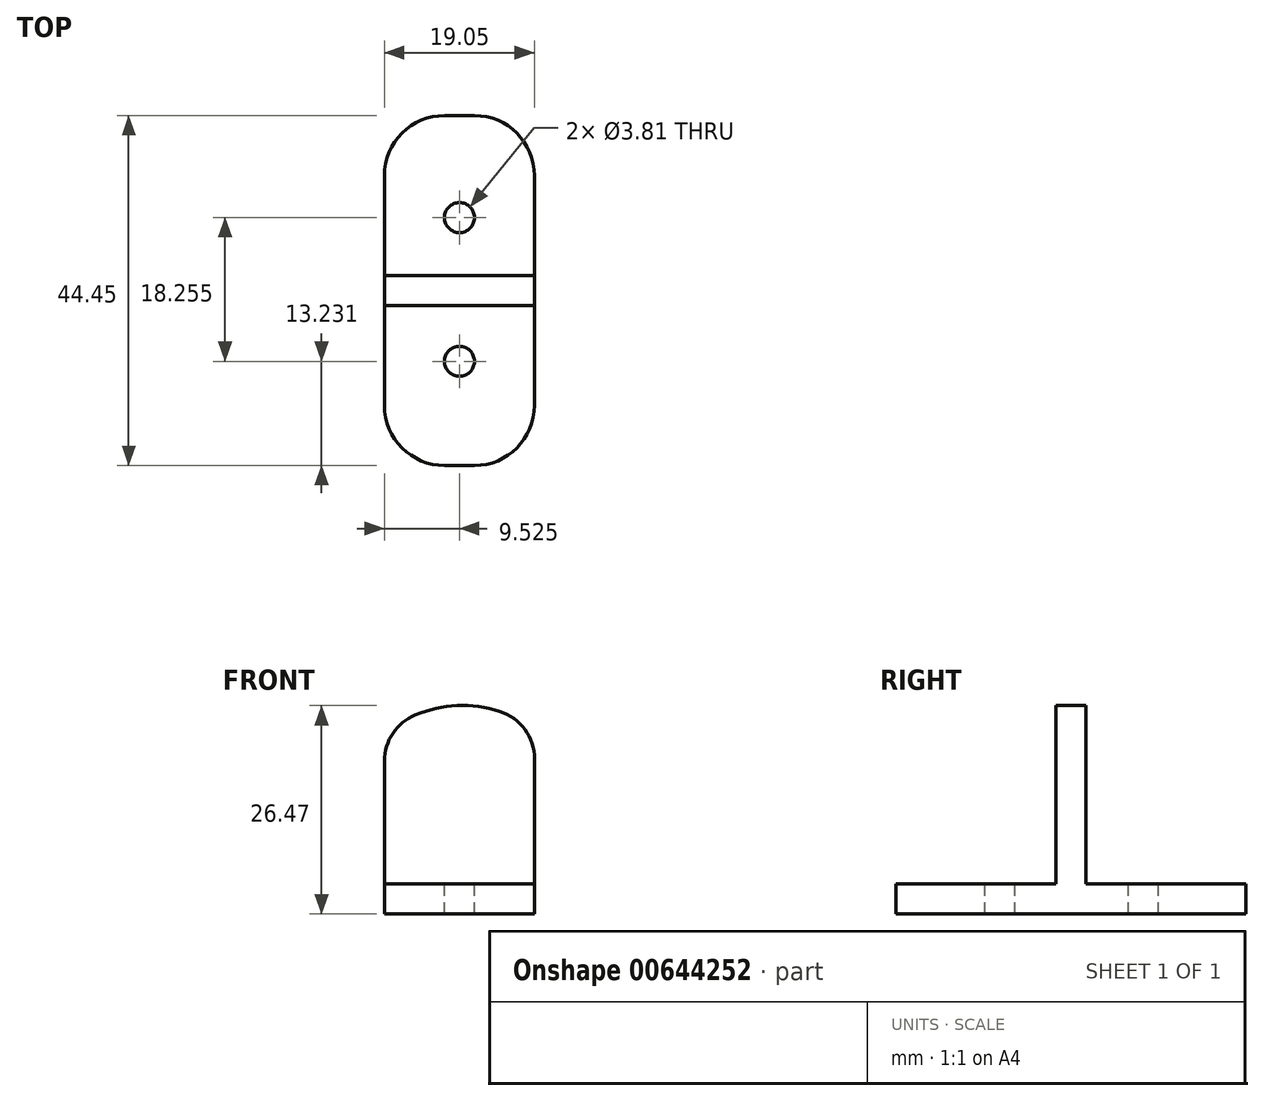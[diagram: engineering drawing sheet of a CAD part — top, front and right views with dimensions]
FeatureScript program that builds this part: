
annotation { "Feature Type Name" : "Feature", "Feature Type Description" : "" }
export const myFeature = defineFeature(function(context is Context, id is Id, definition is map)
    precondition{}
    {
        {
            var Q0;
            Q0=qCreatedBy(makeId("Front.planeOp"),FACE);
            var sketch = newSketch(context, id + "F0", { "sketchPlane" : qUnion([Q0])});
            skLineSegment(sketch, "E0.bottom", {"start": v(0, 0) * mm, "end": v(19.05, 0) * mm});
            skLineSegment(sketch, "E0.top", {"start": v(0, 31.75) * mm, "end": v(19.05, 31.75) * mm});
            skLineSegment(sketch, "E0.left", {"start": v(0, 0) * mm, "end": v(0, 31.75) * mm});
            skLineSegment(sketch, "E0.right", {"start": v(19.05, 0) * mm, "end": v(19.05, 31.75) * mm});
            skArc(sketch, "E1", {"start": v(19.05, 19.69) * mm, "mid": v(9.43, 22.66) * mm, "end": v(0, 19.12) * mm});
            skSolve(sketch);
        }
        {
            var Q0;
            {var subQ0=sQuery(id+"F0.wireOp",EDGE,"E1");var subQ1=sQuery(id+"F0.wireOp",EDGE,"E0.top");var subQ2=makeQuery(id+"F0.imprint","INTERSECT",VERTEX,{"disambiguationData":[OD(0.0)],"derivedFrom":[subQ1,subQ0]});Q0=makeQuery(id+"F0.imprint","IMPRINT",FACE,{"disambiguationData":[TD([[makeQuery(id+"F0.imprint","IMPRINT",EDGE,{"disambiguationData":[TD([[subQ2,-1.0]])],"derivedFrom":subQ1}),1.0]])]});}
            var Q1;
            {var subQ1=sQuery(id+"F0.wireOp",EDGE,"E0.bottom");Q1=makeQuery(id+"F0.imprint","IMPRINT",FACE,{"disambiguationData":[TD([[makeQuery(id+"F0.imprint","IMPRINT",EDGE,{"derivedFrom":subQ1}),1.0]])]});}
            extrude(context, id + "F1", {"entities" : qUnion([Q0, Q1]), "depth" : 3.8 * mm, "offsetDistance" : 25.4 * mm});
        }
        {
            var Q0;
            Q0=makeQuery(id+"F1.opExtrude","SWEPT_EDGE",EDGE,{"disambiguationData":[OSD([sQuery(id+"F0.wireOp",EDGE,"E0.left"),sQuery(id+"F0.wireOp",EDGE,"E1")])]});
            var Q1;
            Q1=makeQuery(id+"F1.opExtrude","SWEPT_EDGE",EDGE,{"disambiguationData":[OSD([sQuery(id+"F0.wireOp",EDGE,"E0.right"),sQuery(id+"F0.wireOp",EDGE,"E1")])]});
            fillet(context, id + "F2", {"entities" : qUnion([Q0, Q1]), "radius" : 6.35 * mm, "tangentPropagation" : true, "allowEdgeOverflow" : false});
        }
        {
            var Q0;
            Q0=makeQuery(id+"F1.opExtrude","SWEPT_FACE",FACE,{"disambiguationData":[OSD([sQuery(id+"F0.wireOp",EDGE,"E0.bottom")])]});
            var sketch = newSketch(context, id + "F3", { "sketchPlane" : qUnion([Q0])});
            skLineSegment(sketch, "E2.bottom", {"start": v(0, 24.13) * mm, "end": v(19.05, 24.13) * mm});
            skLineSegment(sketch, "E2.top", {"start": v(0, -20.32) * mm, "end": v(19.05, -20.32) * mm});
            skLineSegment(sketch, "E2.left", {"start": v(0, 24.13) * mm, "end": v(0, -20.32) * mm});
            skLineSegment(sketch, "E2.right", {"start": v(19.05, 24.13) * mm, "end": v(19.05, -20.32) * mm});
            skPoint(sketch, "E2.middle", {"position": v(9.53, 1.9) * mm});
            skPoint(sketch, "E2.middle.positionSnap0", {"position": v(0, 1.9) * mm});
            skPoint(sketch, "E2.middle.positionSnap1", {"position": v(9.53, 0) * mm});
            skPoint(sketch, "E2.cornerSnap0", {"position": v(0, 1.9) * mm});
            skPoint(sketch, "E2.centerSnap0", {"position": v(0, 1.9) * mm});
            skPoint(sketch, "E2.centerSnap1", {"position": v(9.53, 0) * mm});
            skSolve(sketch);
        }
        {
            var Q0;
            Q0 = qSketchRegion(id + "F3", true);
            extrude(context, id + "F4", {"entities" : qUnion([Q0]), "operationType" : NewBodyOperationType.ADD, "depth" : 3.8 * mm, "offsetDistance" : 25.4 * mm});
        }
        {
            var Q0;
            Q0=makeQuery(id+"F4.opExtrude","SWEPT_EDGE",EDGE,{"disambiguationData":[OSD([sQuery(id+"F3.wireOp",EDGE,"E2.bottom"),sQuery(id+"F3.wireOp",EDGE,"E2.right")])]});
            var Q1;
            Q1=makeQuery(id+"F4.opExtrude","SWEPT_EDGE",EDGE,{"disambiguationData":[OSD([sQuery(id+"F3.wireOp",EDGE,"E2.bottom"),sQuery(id+"F3.wireOp",EDGE,"E2.left")])]});
            var Q2;
            Q2=makeQuery(id+"F4.opExtrude","SWEPT_EDGE",EDGE,{"disambiguationData":[OSD([sQuery(id+"F3.wireOp",EDGE,"E2.top"),sQuery(id+"F3.wireOp",EDGE,"E2.right")])]});
            var Q3;
            Q3=makeQuery(id+"F4.opExtrude","SWEPT_EDGE",EDGE,{"disambiguationData":[OSD([sQuery(id+"F3.wireOp",EDGE,"E2.top"),sQuery(id+"F3.wireOp",EDGE,"E2.left")])]});
            fillet(context, id + "F5", {"entities" : qUnion([Q0, Q1, Q2, Q3]), "radius" : 7.62 * mm, "tangentPropagation" : true, "allowEdgeOverflow" : false});
        }
        {
            var Q0;
            {var subQ0=sQuery(id+"F3.wireOp",EDGE,"E2.bottom");var subQ3=sQuery(id+"F3.wireOp",EDGE,"E2.left");var subQ4=sQuery(id+"F3.wireOp",EDGE,"E2.right");Q0=makeQuery(id+"F4.boolean.opBoolean","SPLIT",FACE,{"disambiguationData":[TD([makeQuery(id+"F4.opExtrude","SWEPT_FACE",FACE,{"disambiguationData":[OSD([subQ0])]})])],"derivedFrom":makeQuery(id+"F4.opExtrude","CAP_FACE",FACE,{"disambiguationData":[OSD([subQ0,sQuery(id+"F3.wireOp",EDGE,"E2.top"),subQ3,subQ4])],"isStart":true})});}
            var sketch = newSketch(context, id + "F6", { "sketchPlane" : qUnion([Q0])});
            skCircle(sketch, "E3", {"center": v(9.53, 7.36) * mm, "radius": 1.9 * mm});
            skPoint(sketch, "E3.centerSnap0", {"position": v(9.53, -3.81) * mm});
            skCircle(sketch, "E4", {"center": v(9.53, -10.9) * mm, "radius": 1.9 * mm});
            skSolve(sketch);
        }
        {
            var Q0;
            Q0 = qSketchRegion(id + "F6", true);
            extrude(context, id + "F7", {"entities" : qUnion([Q0]), "operationType" : NewBodyOperationType.REMOVE, "oppositeDirection" : true, "depth" : 25.4 * mm, "offsetDistance" : 25.4 * mm});
        }
    });
